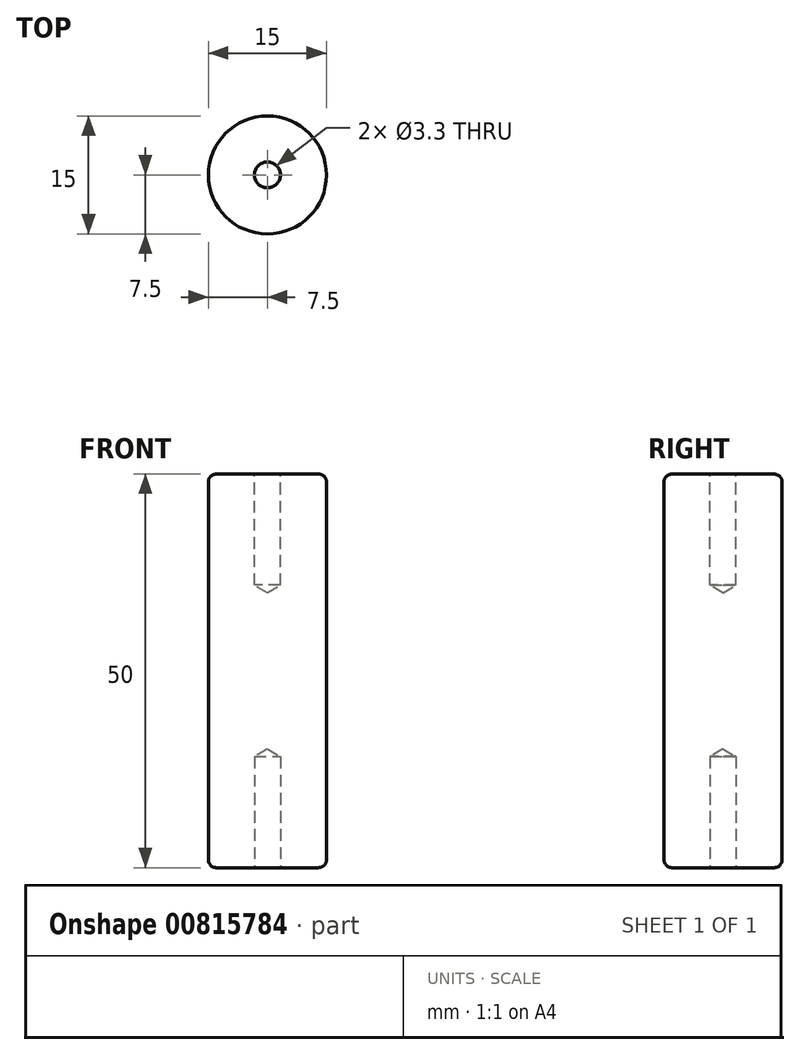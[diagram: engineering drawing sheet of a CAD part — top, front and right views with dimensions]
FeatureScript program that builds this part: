
annotation { "Feature Type Name" : "Feature", "Feature Type Description" : "" }
export const myFeature = defineFeature(function(context is Context, id is Id, definition is map)
    precondition{}
    {
        {
            var Q0;
            Q0=qCreatedBy(makeId("Top.planeOp"),FACE);
            var sketch = newSketch(context, id + "F0", { "sketchPlane" : qUnion([Q0])});
            skCircle(sketch, "E0", {"center": v(0, 0) * mm, "radius": 7.5 * mm});
            skSolve(sketch);
        }
        {
            var Q0;
            Q0=makeQuery(id+"F0.imprint","IMPRINT",FACE,{"disambiguationData":[TD([[makeQuery(id+"F0.imprint","IMPRINT",EDGE,{"derivedFrom":sQuery(id+"F0.wireOp",EDGE,"E0")}),1.0]])]});
            extrude(context, id + "F1", {"entities" : qUnion([Q0]), "depth" : 50 * mm, "offsetDistance" : 25 * mm});
        }
        {
            var Q0;
            Q0=makeQuery(id+"F1.opExtrude","CAP_EDGE",EDGE,{"disambiguationData":[OSD([sQuery(id+"F0.wireOp",EDGE,"E0")])],"isStart":false});
            var Q1;
            Q1=makeQuery(id+"F1.opExtrude","CAP_EDGE",EDGE,{"disambiguationData":[OSD([sQuery(id+"F0.wireOp",EDGE,"E0")])],"isStart":true});
            fillet(context, id + "F2", {"entities" : qUnion([Q0, Q1]), "radius" : 1 * mm, "tangentPropagation" : true, "allowEdgeOverflow" : false});
        }
        {
            var Q0;
            Q0=makeQuery(id+"F1.opExtrude","CAP_FACE",FACE,{"disambiguationData":[OSD([sQuery(id+"F0.wireOp",EDGE,"E0")])],"isStart":false});
            var sketch = newSketch(context, id + "F3", { "sketchPlane" : qUnion([Q0])});
            skPoint(sketch, "E1", {"position": v(0, 0) * mm});
            skCircle(sketch, "E2", {"center": v(0, 0) * mm, "radius": 1.65 * mm});
            skSolve(sketch);
        }
        {
            var Q0;
            Q0=sQuery(id+"F3.wireOp",VERTEX,"E1");
            var Q1;
            Q1=makeQuery(id+"F1.opExtrude","SWEPT_BODY",BODY,{"disambiguationData":[OSD([sQuery(id+"F0.wireOp",EDGE,"E0")])]});
            hole(context, id + "F4", {"style" : HoleStyle.SIMPLE, "endStyle" : HoleEndStyle.BLIND, "standardTappedOrClearance" : lookupTablePath({ "standard" : "ISO", "engagement" : "75%", "pitch" : "0.7 mm", "size" : "M4", "type" : "Tapped" }), "standardBlindInLast" : lookupTablePath({ "standard" : "ISO", "engagement" : "75%", "pitch" : "0.7 mm", "size" : "M4", "type" : "Tapped" }), "holeDiameter" : 3.3 * mm, "majorDiameter" : 4 * mm, "showTappedDepth" : true, "holeDepth" : 14.1 * mm, "isTappedThrough" : true, "tappedDepth" : 12 * mm, "tapClearance" : 3, "locations" : qUnion([Q0]), "scope" : qUnion([Q1])});
        }
        {
            var Q0;
            Q0=makeQuery(id+"F1.opExtrude","CAP_FACE",FACE,{"disambiguationData":[OSD([sQuery(id+"F0.wireOp",EDGE,"E0")])],"isStart":true});
            var sketch = newSketch(context, id + "F5", { "sketchPlane" : qUnion([Q0])});
            skCircle(sketch, "E3", {"center": v(0, 0) * mm, "radius": 1.65 * mm});
            skSolve(sketch);
        }
        {
            var Q0;
            Q0=sQuery(id+"F5.wireOp",VERTEX,"E3.center");
            var Q1;
            Q1=makeQuery(id+"F1.opExtrude","SWEPT_BODY",BODY,{"disambiguationData":[OSD([sQuery(id+"F0.wireOp",EDGE,"E0")])]});
            hole(context, id + "F6", {"style" : HoleStyle.SIMPLE, "endStyle" : HoleEndStyle.BLIND, "standardTappedOrClearance" : lookupTablePath({ "standard" : "ISO", "engagement" : "75%", "pitch" : "0.7 mm", "size" : "M4", "type" : "Tapped" }), "standardBlindInLast" : lookupTablePath({ "standard" : "ISO", "engagement" : "75%", "pitch" : "0.7 mm", "size" : "M4", "type" : "Tapped" }), "holeDiameter" : 3.3 * mm, "majorDiameter" : 4 * mm, "showTappedDepth" : true, "holeDepth" : 14.1 * mm, "isTappedThrough" : true, "tappedDepth" : 12 * mm, "tapClearance" : 3, "locations" : qUnion([Q0]), "scope" : qUnion([Q1])});
        }
    });
